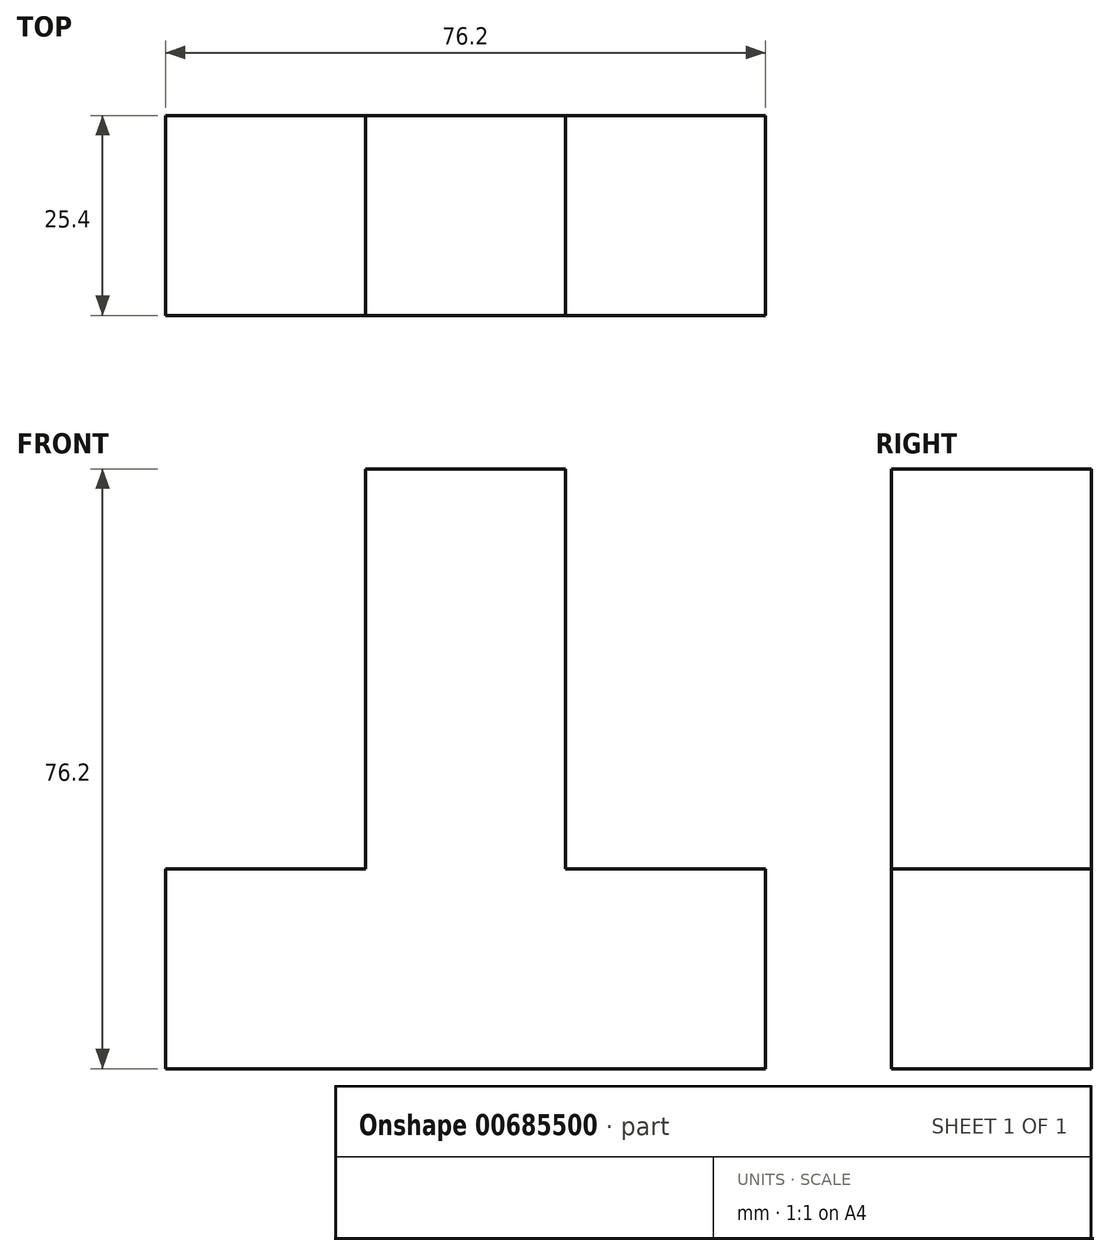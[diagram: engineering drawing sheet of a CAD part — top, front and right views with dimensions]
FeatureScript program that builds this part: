
annotation { "Feature Type Name" : "Feature", "Feature Type Description" : "" }
export const myFeature = defineFeature(function(context is Context, id is Id, definition is map)
    precondition{}
    {
        {
            var Q0;
            Q0=qCreatedBy(makeId("Front.planeOp"),FACE);
            var sketch = newSketch(context, id + "F0", { "sketchPlane" : qUnion([Q0])});
            skLineSegment(sketch, "E0", {"start": v(-39.24, -47.26) * mm, "end": v(36.96, -47.26) * mm});
            skLineSegment(sketch, "E1", {"start": v(-39.24, -47.26) * mm, "end": v(-39.24, -21.86) * mm});
            skLineSegment(sketch, "E2", {"start": v(-39.24, -21.86) * mm, "end": v(-13.84, -21.86) * mm});
            skLineSegment(sketch, "E3", {"start": v(-13.84, -21.86) * mm, "end": v(-13.84, 28.94) * mm});
            skLineSegment(sketch, "E4", {"start": v(-13.84, 28.94) * mm, "end": v(11.56, 28.94) * mm});
            skLineSegment(sketch, "E5", {"start": v(11.56, 28.94) * mm, "end": v(11.56, -21.86) * mm});
            skLineSegment(sketch, "E6", {"start": v(11.56, -21.86) * mm, "end": v(36.96, -21.86) * mm});
            skLineSegment(sketch, "E7", {"start": v(36.96, -21.86) * mm, "end": v(36.96, -47.26) * mm});
            skSolve(sketch);
        }
        {
            var Q0;
            Q0 = qSketchRegion(id + "F0", true);
            extrude(context, id + "F1", {"entities" : qUnion([Q0]), "depth" : 25.4 * mm, "offsetDistance" : 25.4 * mm});
        }
    });
